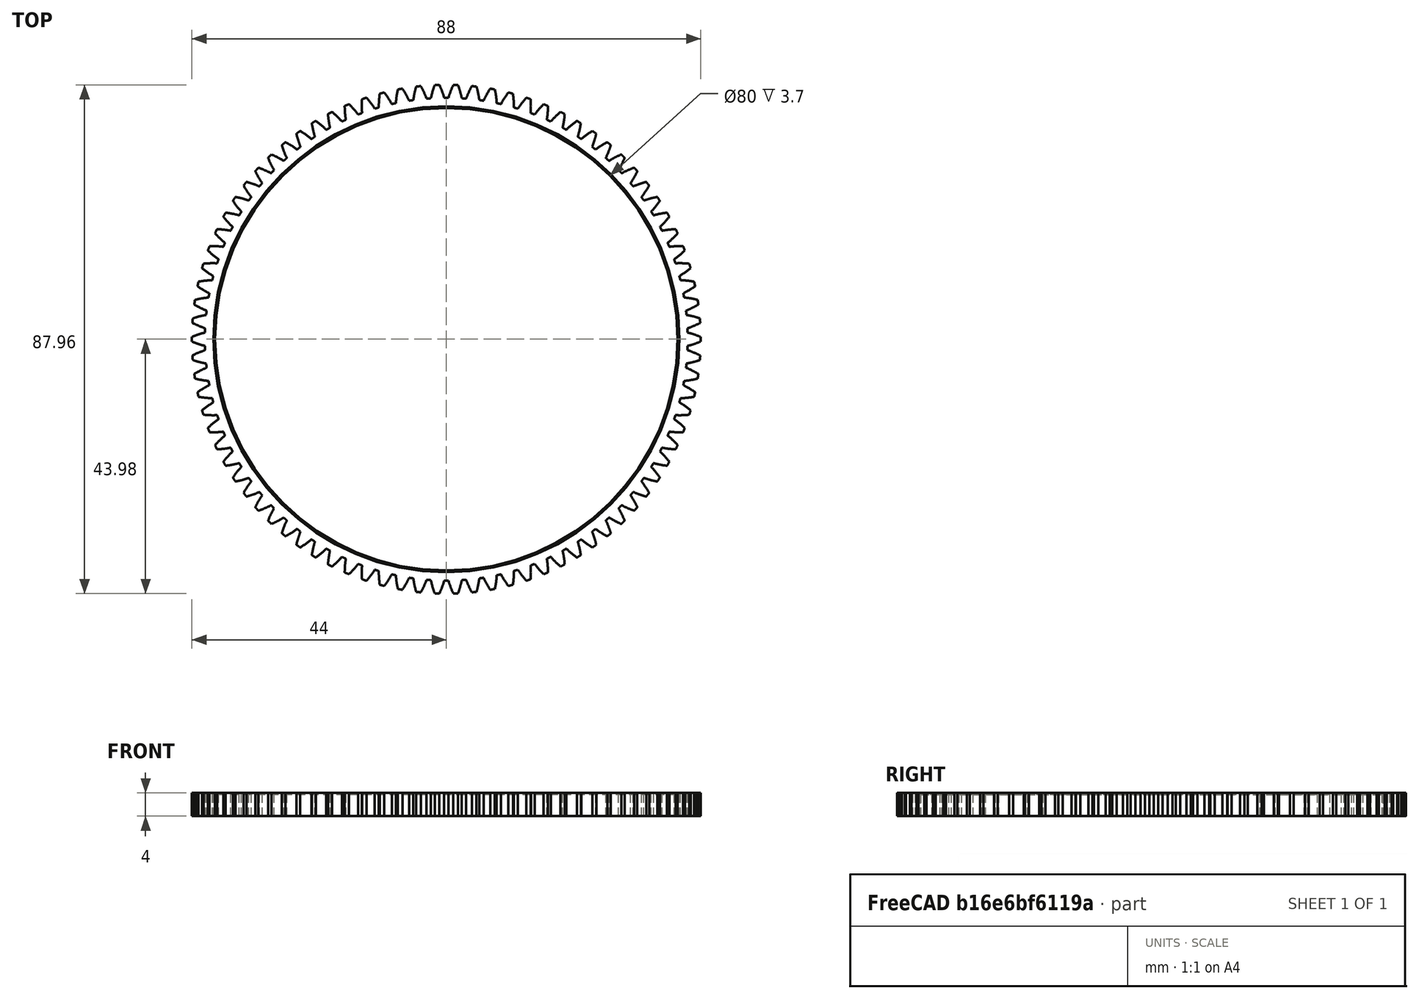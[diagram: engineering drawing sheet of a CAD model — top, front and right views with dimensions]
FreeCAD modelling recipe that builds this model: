
FCSTD DOCUMENT  (FreeCAD 0.19R24276 (Git))
Label: In_gear_t86_temp_v1
License: All rights reserved
LicenseURL: http://en.wikipedia.org/wiki/All_rights_reserved
objects: Sketcher::SketchObject×1, PartDesign::FeaturePython×1, PartDesign::Pocket×1, PartDesign::Chamfer×1, PartDesign::Body×1
note: 7 computed .brp shape members not serialized (recipe doc carries the construction recipe); baked Part::Feature solids carry a one-line shape summary decoded from their .brp

FEATURE [Sketcher::SketchObject] Sketch
  FullyConstrained = true
  MapMode = 5
  Support = -> [XY_Plane]
  sketch-geometry (1):
    g0: Circle CenterX=0 CenterY=0 CenterZ=0 NormalX=0 NormalY=0 NormalZ=1 AngleXU=0 Radius=40
  constraints (2):
    c: Coincident(g0,g-1)
    c: Diameter(g0) = 80
FEATURE [PartDesign::FeaturePython] involutegear  # WARN: FeaturePython — macro-defined, semantics opaque (R4)
  AttacherType = Attacher::AttachEngine3D
  backlash = 0
  beta = 0
  clearance = 0.25
  da = 88
  df = 83.5
  double_helix = false
  dw = 86
  head = 0
  height = 4
  module = 1
  numpoints = 6
  pressure_angle = 20
  properties_from_tool = false
  reversed_backlash = false
  shift = 0
  simple = false
  teeth = 86
  transverse_pitch = 3.14159
  undercut = false
  version = 0.0.3
FEATURE [PartDesign::Pocket] Pocket
  BaseFeature = -> involutegear
  Length = 5
  Length2 = 100
  Profile = -> Sketch
  Reversed = true
  Type = 1
FEATURE [PartDesign::Chamfer] Chamfer
  Angle = 45
  Base = -> Pocket [Edge694]
  BaseFeature = -> Pocket
  ChamferType = 0
  FlipDirection = false
  Size = 0.3
  Size2 = 1
  SupportTransform = false
FEATURE [PartDesign::Body] Body
  Group = -> [Sketch,involutegear,Pocket,Chamfer]
  Origin = -> Origin
  Tip = -> Chamfer
